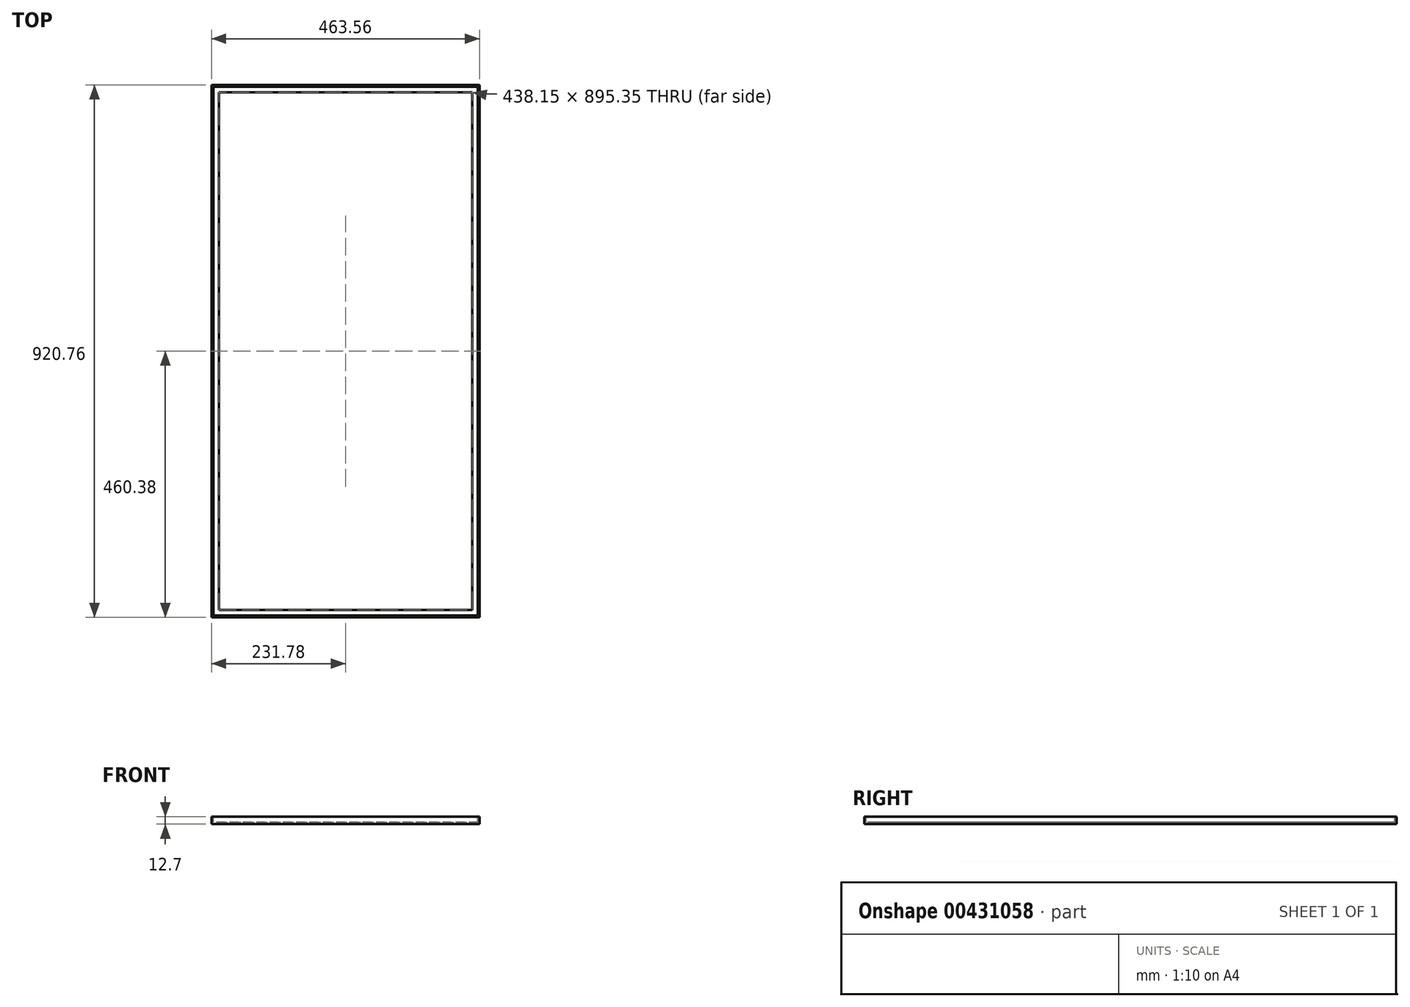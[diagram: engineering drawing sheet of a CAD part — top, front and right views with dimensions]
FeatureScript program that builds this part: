
annotation { "Feature Type Name" : "Feature", "Feature Type Description" : "" }
export const myFeature = defineFeature(function(context is Context, id is Id, definition is map)
    precondition{}
    {
        {
            var Q0;
            Q0=qCreatedBy(makeId("Top.planeOp"),FACE);
            var sketch = newSketch(context, id + "F0", { "sketchPlane" : qUnion([Q0])});
            skLineSegment(sketch, "E0.bottom", {"start": v(228.6, -457.2) * mm, "end": v(-228.6, -457.2) * mm});
            skLineSegment(sketch, "E0.top", {"start": v(228.6, 457.2) * mm, "end": v(-228.6, 457.2) * mm});
            skLineSegment(sketch, "E0.left", {"start": v(228.6, -457.2) * mm, "end": v(228.6, 457.2) * mm});
            skLineSegment(sketch, "E0.right", {"start": v(-228.6, -457.2) * mm, "end": v(-228.6, 457.2) * mm});
            skPoint(sketch, "E0.middle", {"position": v(0, 0) * mm});
            skSolve(sketch);
        }
        {
            var Q0;
            Q0=qCreatedBy(makeId("Front.planeOp"),FACE);
            var sketch = newSketch(context, id + "F1", { "sketchPlane" : qUnion([Q0])});
            skLineSegment(sketch, "E1", {"start": v(231.78, 9.52) * mm, "end": v(231.78, -3.18) * mm});
            skLineSegment(sketch, "E2", {"start": v(231.78, -3.18) * mm, "end": v(219.08, -3.18) * mm});
            skLineSegment(sketch, "E3", {"start": v(219.08, -3.18) * mm, "end": v(219.08, 0) * mm});
            skLineSegment(sketch, "E4", {"start": v(219.08, 0) * mm, "end": v(228.6, 0) * mm});
            skLineSegment(sketch, "E5", {"start": v(228.6, 0) * mm, "end": v(228.6, 9.52) * mm});
            skLineSegment(sketch, "E6", {"start": v(231.78, 9.52) * mm, "end": v(228.6, 9.52) * mm});
            skSolve(sketch);
        }
        {
            var Q0;
            Q0 = qSketchRegion(id + "F1", true);
            var Q1;
            Q1=sQuery(id+"F0.wireOp",EDGE,"E0.left");
            var Q2;
            Q2=sQuery(id+"F0.wireOp",EDGE,"E0.top");
            var Q3;
            Q3=sQuery(id+"F0.wireOp",EDGE,"E0.right");
            var Q4;
            Q4=sQuery(id+"F0.wireOp",EDGE,"E0.bottom");
            sweep(context, id + "F2", {"profiles" : qUnion([Q0]), "path" : qUnion([Q1, Q2, Q3, Q4])});
        }
        {
            var Q0;
            Q0=qCreatedBy(makeId("Front.planeOp"),FACE);
            var sketch = newSketch(context, id + "F3", { "sketchPlane" : qUnion([Q0])});
            skLineSegment(sketch, "E7", {"start": v(-219.08, -3.17) * mm, "end": v(-168.28, -460.38) * mm, "construction": true});
            skLineSegment(sketch, "E8", {"start": v(-168.28, -460.38) * mm, "end": v(168.28, -460.38) * mm, "construction": true});
            skLineSegment(sketch, "E9", {"start": v(168.28, -460.38) * mm, "end": v(219.08, -3.17) * mm, "construction": true});
            skPoint(sketch, "E10", {"position": v(0, -220.43) * mm});
            skPoint(sketch, "E10.positionSnap0", {"position": v(0, -460.38) * mm});
            skSolve(sketch);
        }
    });
